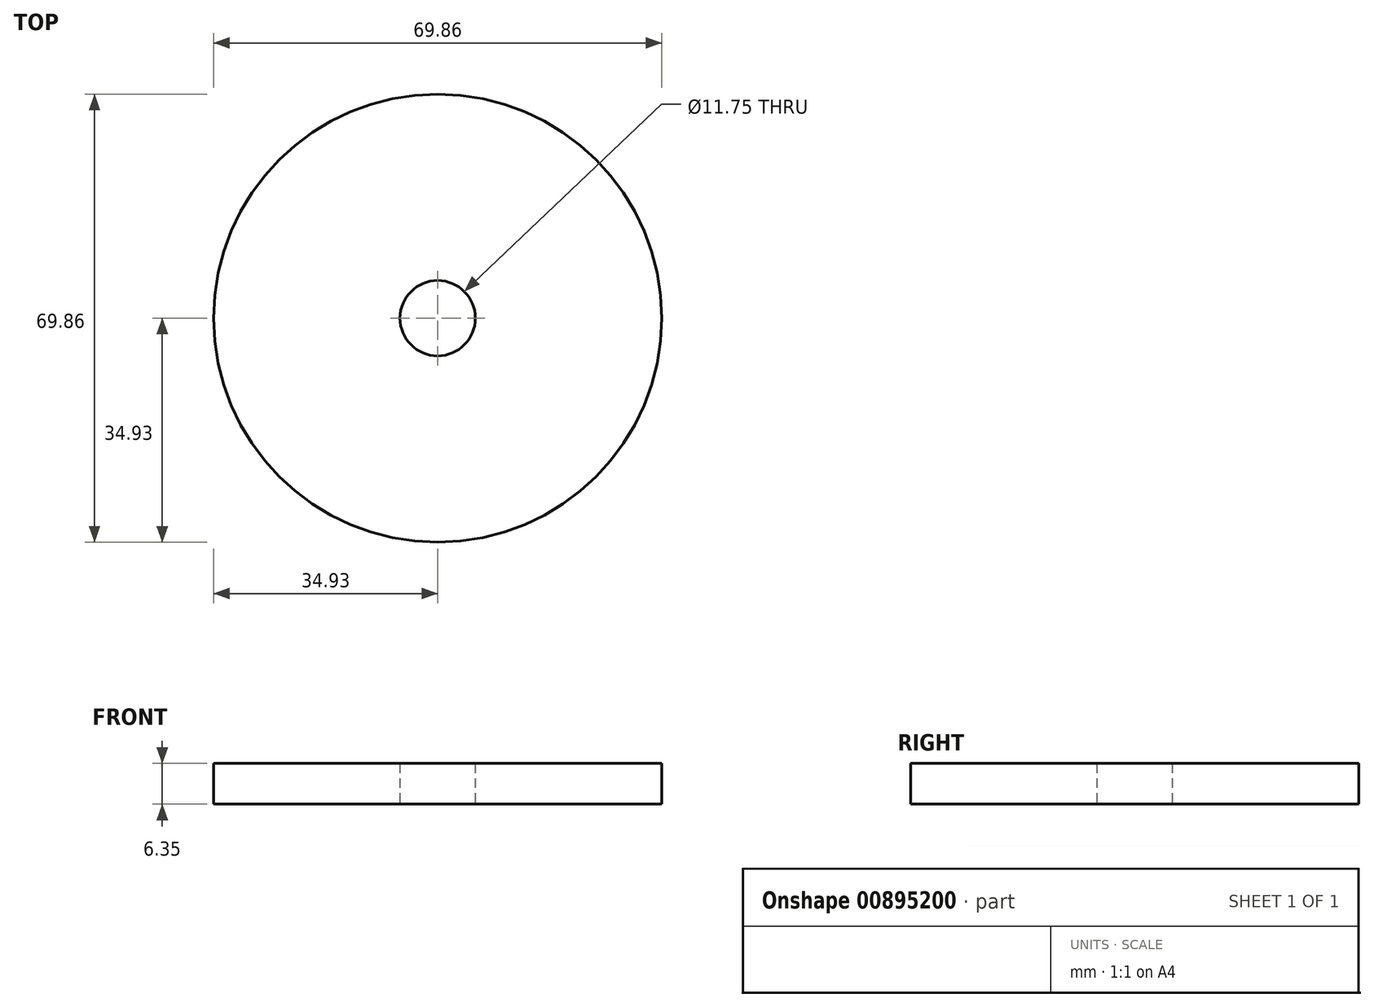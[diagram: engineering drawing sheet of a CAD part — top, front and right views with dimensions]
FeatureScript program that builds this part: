
annotation { "Feature Type Name" : "Feature", "Feature Type Description" : "" }
export const myFeature = defineFeature(function(context is Context, id is Id, definition is map)
    precondition{}
    {
        {
            var Q0;
            Q0=qCreatedBy(makeId("Top.planeOp"),FACE);
            var sketch = newSketch(context, id + "F0", { "sketchPlane" : qUnion([Q0])});
            skCircle(sketch, "E0", {"center": v(0, 0) * mm, "radius": 34.93 * mm});
            skCircle(sketch, "E1", {"center": v(0, 0) * mm, "radius": 5.88 * mm});
            skSolve(sketch);
        }
        {
            var Q0;
            Q0=makeQuery(id+"F0.imprint","IMPRINT",FACE,{"disambiguationData":[TD([[makeQuery(id+"F0.imprint","IMPRINT",EDGE,{"derivedFrom":sQuery(id+"F0.wireOp",EDGE,"E0")}),1.0]])]});
            extrude(context, id + "F1", {"entities" : qUnion([Q0]), "depth" : 6.35 * mm, "offsetDistance" : 25.4 * mm});
        }
    });
